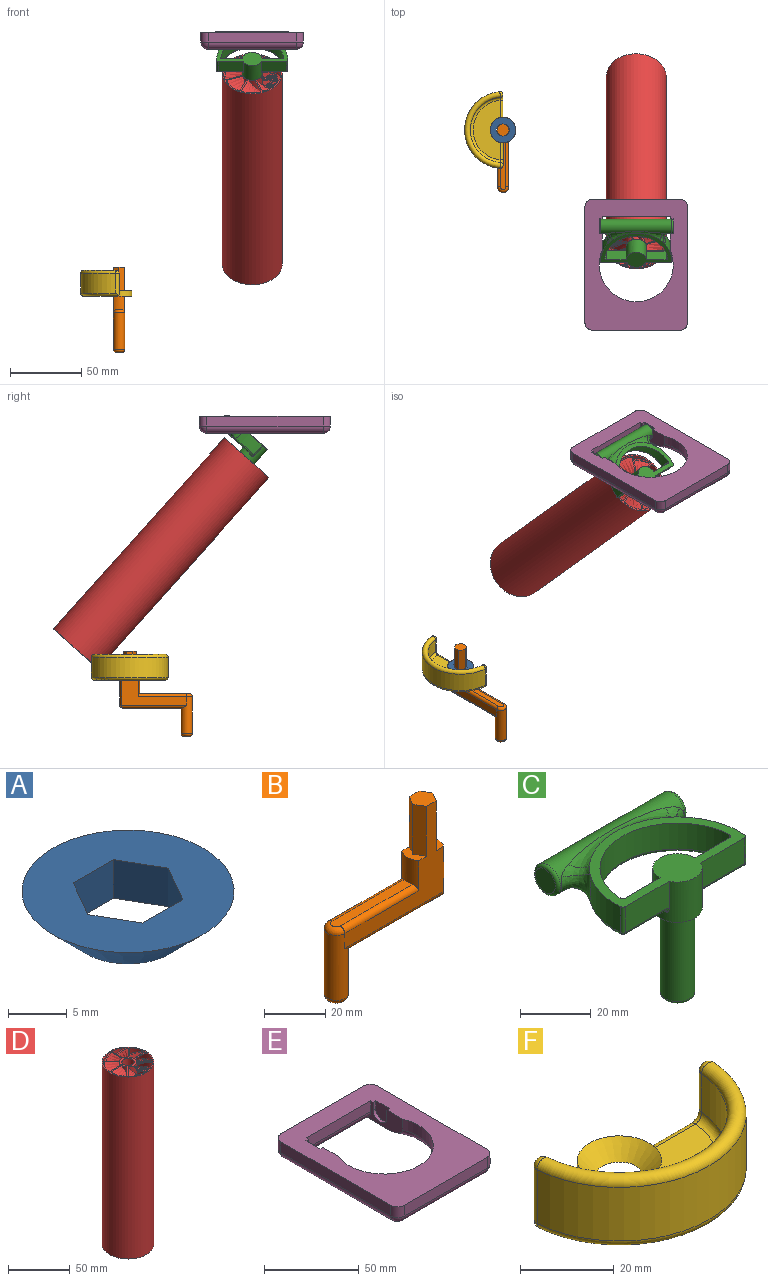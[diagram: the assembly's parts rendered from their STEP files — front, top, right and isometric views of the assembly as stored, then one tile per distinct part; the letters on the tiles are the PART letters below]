
ASSEMBLY  parts=6 mates=4
PART A: 9 faces, bbox 18x18x4 mm
  f0: plane 4.18x4mm, normal (0.87,0.5,0), area 19.3mm2, adj f1,f5,f6,f7
  f1: plane 4.82x4mm, normal (0,1,0), area 19.3mm2, adj f0,f2,f6,f7
  f2: plane 4.18x4mm, normal (-0.87,0.5,0), area 19.3mm2, adj f1,f3,f6,f7
  f3: plane 4.18x4mm, normal (-0.87,-0.5,0), area 19.3mm2, adj f2,f4,f6,f7
  f4: plane 4.82x4mm, normal (0,-1,0), area 19.3mm2, adj f3,f5,f6,f7
  f5: plane 4.18x4mm, normal (0.87,-0.5,0), area 19.3mm2, adj f0,f4,f6,f7
  f6: plane 10x10mm, normal (0,0,-1), area 18.2mm2, adj f0,f1,f2,f3,f4,f5,f8
  f7: plane 18x18mm, normal (0,0,1), area 194.1mm2, adj f0,f1,f2,f3,f4,f5,f8
  f8: cone r=5mm half-angle=45deg, axis (0,0,1), area 248.8mm2, adj f6,f7
PART B: 22 faces, bbox 51.5x8.5x60 mm
  f0: cylinder r=7mm len=12mm, axis (0,0,1), area 85.3mm2, adj f2,f5,f11,f13,f15,f17
  f1: plane 20x3.93mm, normal (-0.87,0.5,0), area 90.6mm2, adj f2,f6,f7,f11
  f2: plane 45.8x38mm, normal (0,1,0), area 504.5mm2, adj f0,f1,f3,f7,f8,f9,f11,f12
  f3: plane 20x3.93mm, normal (0.87,0.5,0), area 90.6mm2, adj f2,f4,f7,f8
  f4: plane 20x3.93mm, normal (0.87,-0.5,0), area 90.6mm2, adj f3,f5,f7,f8
  f5: plane 45.8x38mm, normal (0,-1,0), area 504.5mm2, adj f0,f4,f6,f7,f8,f9,f11,f12
  f6: plane 20x3.93mm, normal (-0.87,-0.5,0), area 90.6mm2, adj f1,f5,f7,f11
  f7: plane 9.06x7.85mm, normal (0,0,1), area 53.4mm2, adj f1,f2,f3,f4,f5,f6
  f8: plane 7.85x4.73mm, normal (0,0,1), area 25.2mm2, adj f2,f3,f4,f5,f9
  f9: cylinder r=7mm len=18mm, axis (0,0,1), area 150mm2, adj f2,f5,f8,f19
  f10: plane 41.58x3.85mm, normal (0,0,-1), area 158.3mm2, adj f12,f18,f19,f20
  f11: plane 7.85x4.73mm, normal (0,0,1), area 25.2mm2, adj f0,f1,f2,f5,f6
  f12: cylinder r=3.92mm len=26mm, axis (0,0,-1), area 548.8mm2, adj f2,f5,f10,f16,f18,f20,f21
  f13: plane 35.2x3.85mm, normal (0,0,1), area 133.2mm2, adj f0,f15,f16,f17
  f14: plane 3.85x3.85mm, normal (0,0,-1), area 11.6mm2, adj f21
  f15: cylinder r=2mm len=34.2mm, axis (1,0,0), area 106.2mm2, adj f0,f5,f13,f16
  f16: torus R=1.93mm, axis (0,0,-1), area 31.6mm2, adj f12,f13,f15,f17
  f17: cylinder r=2mm len=34.2mm, axis (1,0,0), area 106.2mm2, adj f0,f2,f13,f16
  f18: cylinder r=2mm len=45.8mm, axis (1,0,0), area 136.5mm2, adj f2,f10,f12,f19
  f19: torus R=5mm, axis (0,0,-1), area 21.1mm2, adj f9,f10,f18,f20
  f20: cylinder r=2mm len=45.8mm, axis (-1,0,0), area 136.5mm2, adj f5,f10,f12,f19
  f21: torus R=1.93mm, axis (0,0,-1), area 63.1mm2, adj f12,f14
PART C: 49 faces, bbox 55.2x40.5x46.5 mm
  f0: bspline ~40.76x8.77mm, area 119mm2, adj f1,f12,f20,f25,f38
  f1: bspline ~8.79x8.41mm, area 22.2mm2, adj f0,f20,f26,f38
  f2: bspline ~40.76x8.77mm, area 120.1mm2, adj f3,f16,f20,f28
  f3: bspline ~8.79x8.41mm, area 24.9mm2, adj f2,f16,f20,f27
  f4: cylinder r=25mm len=17.37mm, axis (0,0,-1), area 157.7mm2, adj f16,f26,f36,f39
  f5: plane 14.25x11mm, normal (0,1,0), area 140.1mm2, adj f8,f12,f16,f17,f43,f44
  f6: plane 17.59x9.54mm, normal (0,-1,0), area 158.6mm2, adj f8,f16,f39,f41,f42
  f7: cylinder r=25mm len=17.37mm, axis (0,0,-1), area 157.7mm2, adj f16,f27,f33,f47
  f8: cylinder r=7mm len=14mm, axis (0,0,-1), area 549.6mm2, adj f5,f6,f9,f13,f14,f16,f17,f18
  f9: plane 14x14mm, normal (0,0,-1), area 80mm2, adj f8,f10
  f10: cylinder r=4.85mm len=29mm, axis (0,0,1), area 883.7mm2, adj f9,f19
  f11: plane 7.7x7.7mm, normal (0,0,-1), area 46.6mm2, adj f19
  f12: plane 49.08x28.08mm, normal (0,0,-1), area 162.8mm2, adj f0,f5,f17,f18,f25,f29,f30,f32
  f13: plane 13.98x9.23mm, normal (0,1,0), area 125.9mm2, adj f8,f16,f30,f31,f45
  f14: plane 17.59x9.54mm, normal (0,-1,0), area 158.6mm2, adj f8,f16,f34,f35,f47
  f15: cylinder r=22mm len=43.95mm, axis (0,0,-1), area 603.2mm2, adj f16,f29,f43,f45
  f16: plane 50.9x32.9mm, normal (0,0,1), area 484.7mm2, adj f2,f3,f4,f5,f6,f7,f8,f13
  f17: torus R=8mm, axis (0,0,1), area 3.4mm2, adj f5,f8,f12,f42
  f18: torus R=8mm, axis (0,0,1), area 1.7mm2, adj f8,f12,f31,f35
  f19: torus R=3.85mm, axis (0,0,1), area 44.3mm2, adj f10,f11
  f20: cylinder r=5mm len=50mm, axis (-1,0,0), area 1000.9mm2, adj f0,f1,f2,f3,f23,f24,f25,f26
  f21: plane 8x8mm, normal (1,0,0), area 50.3mm2, adj f24
  f22: plane 8x8mm, normal (-1,0,0), area 50.3mm2, adj f23
  f23: torus R=4mm, axis (-1,0,0), area 45.8mm2, adj f20,f22
  f24: torus R=4mm, axis (1,0,0), area 45.8mm2, adj f20,f21
  f25: bspline ~8.79x6.68mm, area 23.2mm2, adj f0,f12,f20,f27,f32
  f26: bspline ~12.37x9.52mm, area 65mm2, adj f1,f4,f20,f28,f37
  f27: bspline ~11.63x9.51mm, area 65mm2, adj f3,f7,f20,f25,f32
  f28: bspline ~8.79x8.41mm, area 24.7mm2, adj f2,f16,f20,f26
  f29: torus R=23mm, axis (0,0,1), area 108.7mm2, adj f12,f15,f44,f46
  f30: cylinder r=1mm len=15.04mm, axis (-1,0,0), area 22.1mm2, adj f12,f13,f31,f46
  f31: bspline ~2.36x2.3mm, area 2.1mm2, adj f8,f13,f18,f30
  f32: bspline ~4.99x3.42mm, area 3.8mm2, adj f12,f25,f27,f33
  f33: torus R=24mm, axis (0,0,1), area 27.9mm2, adj f7,f12,f32,f48
  f34: cylinder r=1mm len=16.17mm, axis (1,0,0), area 25.4mm2, adj f12,f14,f35,f48
  f35: bspline ~2.41x2.37mm, area 2.3mm2, adj f8,f14,f18,f34
  f36: torus R=24mm, axis (0,0,1), area 27.9mm2, adj f4,f12,f37,f40
  f37: bspline ~4.19x3.15mm, area 2.6mm2, adj f12,f26,f36,f38
  f38: bspline ~5.84x5.81mm, area 4.2mm2, adj f0,f1,f12,f37
  f39: cylinder r=1mm len=9mm, axis (0,0,-1), area 13.4mm2, adj f4,f6,f16,f40
  f40: sphere r=1mm, area 1.5mm2, adj f36,f39,f41
  f41: cylinder r=1mm len=16.17mm, axis (1,0,0), area 25.4mm2, adj f6,f12,f40,f42
  f42: bspline ~2.41x2.37mm, area 2.3mm2, adj f6,f8,f17,f41
  f43: cylinder r=1mm len=9mm, axis (0,0,-1), area 14.6mm2, adj f5,f15,f16,f44
  f44: bspline ~2.35x2.28mm, area 2.1mm2, adj f5,f12,f29,f43
  f45: cylinder r=1mm len=9mm, axis (0,0,-1), area 14.6mm2, adj f13,f15,f16,f46
  f46: bspline ~2.05x2mm, area 1.2mm2, adj f29,f30,f45
  f47: cylinder r=1mm len=9mm, axis (0,0,-1), area 13.4mm2, adj f7,f14,f16,f48
  f48: sphere r=1mm, area 1.5mm2, adj f33,f34,f47
PART D: 59 faces, bbox 42.5x42.5x184.9 mm
  f0: cylinder r=20mm len=180mm, axis (0,0,-1), area 1969.5mm2, adj f11,f12,f37,f51
  f1: cylinder r=7mm len=180mm, axis (0,0,-1), area 808.3mm2, adj f11,f12,f33,f34
  f2: cylinder r=20mm len=180mm, axis (0,0,-1), area 1969.5mm2, adj f11,f12,f36,f39
  f3: cylinder r=7mm len=180mm, axis (0,0,-1), area 808.3mm2, adj f11,f12,f31,f32
  f4: cylinder r=20mm len=180mm, axis (0,0,-1), area 1969.5mm2, adj f11,f12,f38,f41
  f5: cylinder r=7mm len=180mm, axis (0,0,-1), area 808.3mm2, adj f11,f12,f29,f30
  f6: cylinder r=20mm len=180mm, axis (0,0,-1), area 1969.5mm2, adj f11,f12,f40,f43
  f7: cylinder r=7mm len=180mm, axis (0,0,-1), area 808.3mm2, adj f11,f12,f27,f28
  f8: cylinder r=20mm len=180mm, axis (0,0,-1), area 1969.5mm2, adj f11,f12,f42,f45
  f9: cylinder r=7mm len=180mm, axis (0,0,-1), area 808.3mm2, adj f11,f12,f25,f26
  f10: bspline ~180x40.77mm, area 3757.6mm2, adj f11,f12,f14,f48
  f11: plane 42.46x42.46mm, normal (0,0,-1), area 331.8mm2, adj f0,f1,f2,f3,f4,f5,f6,f7
  f12: plane 42.47x42.47mm, normal (0,0,1), area 313.7mm2, adj f0,f1,f2,f3,f4,f5,f6,f7
  f13: bspline ~180x38.34mm, area 3755.7mm2, adj f11,f12,f16,f49
  f14: cylinder r=7mm len=180mm, axis (0,0,-1), area 808.3mm2, adj f10,f11,f12,f23
  f15: cylinder r=20mm len=180mm, axis (0,0,-1), area 1969.5mm2, adj f11,f12,f48,f50
  f16: cylinder r=7mm len=180mm, axis (0,0,-1), area 808.3mm2, adj f11,f12,f13,f24
  f17: cylinder r=20mm len=180mm, axis (0,0,-1), area 1969.5mm2, adj f11,f12,f44,f47
  f18: cylinder r=5mm len=160mm, axis (0,0,-1), area 5026.5mm2, adj f12,f58
  f19: cylinder r=7mm len=180mm, axis (0,0,-1), area 808.3mm2, adj f11,f12,f20,f35
  f20: bspline ~180x41.03mm, area 3757.6mm2, adj f11,f12,f19,f51
  f21: cylinder r=20mm len=180mm, axis (0,0,-1), area 1969.5mm2, adj f11,f12,f46,f49
  f22: cylinder r=21mm len=180mm, axis (0,0,-1), area 23750.4mm2, adj f11,f12
  f23: bspline ~180x40.98mm, area 3755.7mm2, adj f11,f12,f14,f50
  f24: bspline ~180x41.03mm, area 3757.6mm2, adj f11,f12,f16,f46
  f25: bspline ~180x40.98mm, area 3755.7mm2, adj f9,f11,f12,f47
  f26: bspline ~180x40.77mm, area 3757.6mm2, adj f9,f11,f12,f44
  f27: bspline ~180x38.34mm, area 3755.7mm2, adj f7,f11,f12,f45
  f28: bspline ~180x41.03mm, area 3757.6mm2, adj f7,f11,f12,f42
  f29: bspline ~180x40.98mm, area 3755.7mm2, adj f5,f11,f12,f43
  f30: bspline ~180x40.77mm, area 3757.6mm2, adj f5,f11,f12,f40
  f31: bspline ~180x38.34mm, area 3755.7mm2, adj f3,f11,f12,f41
  f32: bspline ~180x41.03mm, area 3757.6mm2, adj f3,f11,f12,f38
  f33: bspline ~180x40.98mm, area 3755.7mm2, adj f1,f11,f12,f39
  f34: bspline ~180x40.77mm, area 3757.6mm2, adj f1,f11,f12,f36
  f35: bspline ~180x38.34mm, area 3755.7mm2, adj f11,f12,f19,f37
  f36: bspline ~183.47x40.03mm, area 521.3mm2, adj f2,f11,f12,f34
  f37: bspline ~183.29x40.02mm, area 528.5mm2, adj f0,f11,f12,f35
  f38: bspline ~183.47x40.03mm, area 521.3mm2, adj f4,f11,f12,f32
  f39: bspline ~183.29x40.02mm, area 528.5mm2, adj f2,f11,f12,f33
  f40: bspline ~183.47x40.03mm, area 521.3mm2, adj f6,f11,f12,f30
  f41: bspline ~183.29x40.02mm, area 528.5mm2, adj f4,f11,f12,f31
  f42: bspline ~183.47x40.03mm, area 521.3mm2, adj f8,f11,f12,f28
  f43: bspline ~183.29x40.02mm, area 528.5mm2, adj f6,f11,f12,f29
  f44: bspline ~183.47x40.03mm, area 521.3mm2, adj f11,f12,f17,f26
  f45: bspline ~183.29x40.02mm, area 528.5mm2, adj f8,f11,f12,f27
  f46: bspline ~183.47x40.03mm, area 521.3mm2, adj f11,f12,f21,f24
  f47: bspline ~183.29x40.02mm, area 528.5mm2, adj f11,f12,f17,f25
  f48: bspline ~183.47x40.03mm, area 521.3mm2, adj f10,f11,f12,f15
  f49: bspline ~183.29x40.02mm, area 528.5mm2, adj f11,f12,f13,f21
  f50: bspline ~183.29x40.02mm, area 528.5mm2, adj f11,f12,f15,f23
  f51: bspline ~183.47x40.03mm, area 521.3mm2, adj f0,f11,f12,f20
  f52: plane 20x4.82mm, normal (0,1,0), area 96.4mm2, adj f11,f53,f57,f58
  f53: plane 20x4.18mm, normal (-0.87,0.5,0), area 96.4mm2, adj f11,f52,f54,f58
  f54: plane 20x4.18mm, normal (-0.87,-0.5,0), area 96.4mm2, adj f11,f53,f55,f58
  f55: plane 20x4.82mm, normal (0,-1,0), area 96.4mm2, adj f11,f54,f56,f58
  f56: plane 20x4.18mm, normal (0.87,-0.5,0), area 96.4mm2, adj f11,f55,f57,f58
  f57: plane 20x4.18mm, normal (0.87,0.5,0), area 96.4mm2, adj f11,f52,f56,f58
  f58: plane 10x10mm, normal (0,0,1), area 18.2mm2, adj f18,f52,f53,f54,f55,f56,f57
PART E: 33 faces, bbox 74.8x92x12 mm
  f0: plane 62x41mm, normal (0,0,-1), area 482.3mm2, adj f1,f2,f22,f23,f27,f31,f32
  f1: plane 29x12mm, normal (-1,0,0), area 187.1mm2, adj f0,f3,f4,f5,f12,f13,f14,f31
  f2: plane 29x12mm, normal (1,0,0), area 187.1mm2, adj f0,f3,f4,f5,f15,f16,f17,f31
  f3: plane 92x72mm, normal (0,0,1), area 3840.2mm2, adj f1,f2,f4,f5,f6,f7,f8,f9
  f4: plane 48x7mm, normal (0,-1,0), area 336mm2, adj f1,f2,f3,f32
  f5: cylinder r=26mm len=52mm, axis (0,0,1), area 715.5mm2, adj f1,f2,f3,f31
  f6: plane 62x7mm, normal (0,-1,0), area 434mm2, adj f3,f24,f28,f30
  f7: plane 82x7mm, normal (1,0,0), area 574mm2, adj f3,f21,f27,f30
  f8: plane 62x7mm, normal (0,1,0), area 434mm2, adj f3,f19,f21,f22
  f9: plane 82x7mm, normal (-1,0,0), area 574mm2, adj f3,f19,f23,f24
  f10: plane 62x41mm, normal (0,0,-1), area 1032.5mm2, adj f23,f27,f28,f31
  f11: plane 10.4x10.2mm, normal (-1,0,0), area 94.5mm2, adj f3,f12,f13,f14
  f12: plane 5x2mm, normal (0,-1,0), area 10mm2, adj f1,f3,f11,f14
  f13: plane 5x2mm, normal (0,1,0), area 10mm2, adj f1,f3,f11,f14
  f14: cylinder r=5.2mm len=10.4mm, axis (1,0,0), area 32.7mm2, adj f1,f11,f12,f13
  f15: plane 5x2mm, normal (0,1,0), area 10mm2, adj f2,f3,f16,f18
  f16: cylinder r=5.2mm len=10.4mm, axis (1,0,0), area 32.7mm2, adj f2,f15,f17,f18
  f17: plane 5x2mm, normal (0,-1,0), area 10mm2, adj f2,f3,f16,f18
  f18: plane 10.4x10.2mm, normal (1,0,0), area 94.5mm2, adj f3,f15,f16,f17
  f19: cylinder r=5mm len=7mm, axis (0,0,1), area 55mm2, adj f3,f8,f9,f20
  f20: sphere r=5mm, area 39.3mm2, adj f19,f22,f23
  f21: cylinder r=5mm len=7mm, axis (0,0,-1), area 55mm2, adj f3,f7,f8,f25
  f22: cylinder r=5mm len=62mm, axis (1,0,0), area 486.9mm2, adj f0,f8,f20,f25
  f23: cylinder r=5mm len=82mm, axis (0,1,0), area 644mm2, adj f0,f9,f10,f20,f26
  f24: cylinder r=5mm len=7mm, axis (0,0,-1), area 55mm2, adj f3,f6,f9,f26
  f25: sphere r=5mm, area 39.3mm2, adj f21,f22,f27
  f26: sphere r=5mm, area 39.3mm2, adj f23,f24,f28
  f27: cylinder r=5mm len=82mm, axis (0,-1,0), area 644mm2, adj f0,f7,f10,f25,f29
  f28: cylinder r=5mm len=62mm, axis (-1,0,0), area 486.9mm2, adj f6,f10,f26,f29
  f29: sphere r=5mm, area 39.3mm2, adj f27,f28,f30
  f30: cylinder r=5mm len=7mm, axis (0,0,1), area 55mm2, adj f3,f6,f7,f29
  f31: torus R=31mm, axis (0,0,1), area 914.7mm2, adj f0,f1,f2,f5,f10
  f32: cylinder r=5mm len=48mm, axis (-1,0,0), area 377mm2, adj f0,f1,f2,f4
PART F: 20 faces, bbox 58.4x38.2x18 mm
  f0: cylinder r=23mm len=45.85mm, axis (0,0,-1), area 685.7mm2, adj f9,f11,f14,f16
  f1: plane 15.92x6mm, normal (0,1,0), area 35.3mm2, adj f5,f6,f10,f11,f13
  f2: cylinder r=27mm len=53.83mm, axis (0,0,-1), area 1127mm2, adj f9,f11,f14,f15
  f3: plane 4.02x4.01mm, normal (0,1,0), area 3.4mm2, adj f14,f18,f19
  f4: plane 41.81x19mm, normal (0,0,1), area 517.3mm2, adj f7,f10,f16,f19
  f5: cylinder r=9mm len=18mm, axis (0,0,1), area 115.7mm2, adj f1,f6,f7,f10,f19
  f6: plane 49.92x34mm, normal (0,0,-1), area 998.3mm2, adj f1,f5,f7,f11,f15,f19
  f7: cone r=9mm half-angle=45deg, axis (0,0,1), area 248.8mm2, adj f4,f5,f6
  f8: sphere r=2mm, area 12.6mm2, adj f9,f11
  f9: torus R=25mm, axis (0,0,-1), area 468.3mm2, adj f0,f2,f8,f12
  f10: cylinder r=2mm len=12.13mm, axis (-1,0,0), area 37.6mm2, adj f1,f4,f5,f13
  f11: cylinder r=2mm len=16mm, axis (0,0,-1), area 80.3mm2, adj f0,f1,f2,f6,f8,f13,f15
  f12: sphere r=2mm, area 12.6mm2, adj f9,f14
  f13: bspline ~4.92x4.7mm, area 13.2mm2, adj f1,f10,f11,f16
  f14: cylinder r=2mm len=14mm, axis (0,0,-1), area 76mm2, adj f0,f2,f3,f12,f17,f18
  f15: torus R=25mm, axis (0,0,-1), area 250.2mm2, adj f2,f6,f11,f17
  f16: torus R=21mm, axis (0,0,-1), area 207.9mm2, adj f0,f4,f13,f18
  f17: sphere r=2mm, area 6.6mm2, adj f14,f15,f19
  f18: bspline ~4.9x4.7mm, area 13.2mm2, adj f3,f14,f16,f19
  f19: cylinder r=2mm len=16.15mm, axis (1,0,0), area 87.7mm2, adj f3,f4,f5,f6,f17,f18
PLACE A rot(axis=(-0.36,-0.74,0.57),0.1deg) t=(-100.66,94.07,5.25)mm
PLACE B rot(axis=(0,0,1),90.1deg) t=(-100.65,94.07,1.58)mm
PLACE C rot(axis=(1,0,0),41.8deg) t=(-7.05,131.94,23.25)mm
PLACE D rot(axis=(0.46,0.32,-0.83),78.8deg) t=(-7.05,131.94,23.25)mm
PLACE E t=(-7.05,-0.92,-7.25)mm fixed
PLACE F rot(axis=(0,0,-1),89.9deg) t=(-100.66,94.07,5.25)mm
MATE revolute C.f8 <-> D.f18  axis (0,0.67,-0.75) through (-7.05,11.95,157.43)mm
MATE cylindrical B.f0 <-> A.f8  axis (0,0,1) through (-100.65,94.07,1.58)mm
MATE revolute C.f20 <-> E.f11  axis (1,0,0) through (18.95,26.08,182.13)mm
MATE cylindrical F.f0 <-> A.f8  axis (0,0,-1) through (-100.65,94.07,1.25)mm
